# Revit family: Lighting_Pendants_Zero_Lumo-Wire
name_source: partatom
category: Lighting Fixtures
units: mm (PartAtom-declared; Revit-internal decimal feet)

## family parameters
Always vertical = Yes
Cut with Voids When Loaded = No
Light Source = Yes
OmniClass Number = 23.80.70.00
OmniClass Title = Lighting
Part Type = Normal
Room Calculation Point = No
Round Connector Dimension = Use Diameter
Shared = No
Work Plane-Based = No

## types (2) — shared parameters
AssetType = Fixed
BIMObjectName = Lighting_Pendant_Zero_Lumo-Wire
Brand = Zero
Category = Pendant Fixtures
Color = Red
Color Filter = 16777215
Designer = Thomas Bernstrand 2023
Dimming Lamp Color Temperature Shift = <None>
DurationUnit = Years
Emit from Line Length = 500 mm  [stored 1.64042 ft]
Features = Delivered with 2 m black cable 3x1,5mm2 when DALI 5x1,5mm2.
Finish = Other colours on request.
HasProtectiveEarth = Yes
IP_Code = IP65
IfcExportAs = IfcLightFixtureType
IfcExportType = NOTDEFINED
Lamp = Can be delivered with 2700K, 4000K on request.
LensMaterial = Glass
Light Source Symbol Length = 300 mm
LightFixtureMainMaterial = Black RAL 9005
LightFixtureMountingType = Surface
LightFixturePlacingType = Table
Manufacturer = Zero
ManufacturerName = Zero
ManufacturerURL = https://www.zerolighting.com
ManufacturersSpecificInformation = DCL-plug or terminal block 5x2,5mm2
Material = Metal
NBSDescription = General purpose luminaires
NBSReference = 90-60-50/405
Name = Compose-Wire
NominalCurrent = 0 A
NominalDiameter = 120 mm  [stored 0.393701 ft]
NominalFrequencyRange = 50 Hz
NominalLength = 250 mm  [stored 0.82021 ft]
NominalRadius = 60 mm  [stored 0.19685 ft]
NominalVoltage = 230 V
NominalVoltageCalc = 0 V
NominalWidth = 250 mm  [stored 0.82021 ft]
NumberOfPoles = 1
PhaseAngle = 0.00°
Revision = 1
Shape = Sculptured
Size = 250x250x322 mm
Spot Beam Angle = 90.00°
Spot Field Angle = 90.00°
Tilt Angle = 90.00°
TotalWattage = 22 W
Uniclass2 = 90-65-49/434
Uniclass2015Description = Suspended luminaires
Uniclass2015Reference = Pr_70_70_49_86
UsageCurrent = 0 A
Version = 2
VersionDate = 31/08/2023
WarrantyDurationUnit = Years
zero-valued in all types: Default Elevation, DefaultElevation, ElectricalDeviceNominalPower, MaintenanceFactor, NumberOfSources

## per-type parameters (varying)
| type | ArticleNumber | Model | ModelNumber |
| Compose wire - Black Matt acrylic, on/off | 12138106-30 | Lumo wire - Black Matt acrylic, on/off | 12138106-30 |
| Compose wire - Black Matt acrylic, Dali | 12138106D30 | Lumo wire - Black Matt acrylic, Dali | 12138106D30 |

note: [stored X ft] marks values corroborated as IEEE doubles in the binary element streams (Revit-internal decimal feet)

## geometry (parser evidence)
native form markers: Sweep x5
no freeform markers — native parametric forms only
